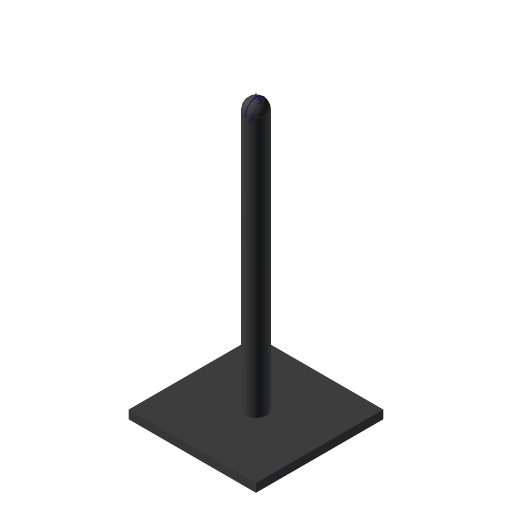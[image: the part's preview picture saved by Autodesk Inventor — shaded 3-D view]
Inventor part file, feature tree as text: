
AUTODESK INVENTOR PART (.ipt)
format: ipt  version: 2023.4 (Build 274418000, 418)  size: 112,640 bytes
history: native  units: in
note: dims shown in document units (in); Inventor stores cm internally (conversion verified against a paired STEP export)
features: sketch x4, extrude x2, revolve x1
ambient origin geometry x8: Origin, YZ Plane, XZ Plane, XY Plane, X Axis, Y Axis, Z Axis, Center Point
bodies: Solid1 (feature_tree)
feature tree (7):
  extrude  "Extrusion1"  Depth=1.1811in
  extrude  "Extrusion2"  TaperAngle=0.0deg  [1 undecoded]
  sketch  "Sketch3"  dims[d4=0.0787in d5=0.0in d6=0.1969in]
  revolve  "Revolution3"  [1 undecoded]
  sketch  "Sketch1"  dims[d0=1.1811in d1=1.1811in]
  sketch  "Sketch2"  dims[d2=0.0in d3=0.0in]
  sketch  "Sketch4"  dims[d7=2.4171in d8=0.0in d9=0.1969in d12=90.0deg d13=0.0344in d14=0.0197in d15=0.0344in]
note: 2 required parameter values undecoded (feature->parameter linkage not recoverable at this tier; creation-order binding heuristic only, values carry confidence <= 0.55)